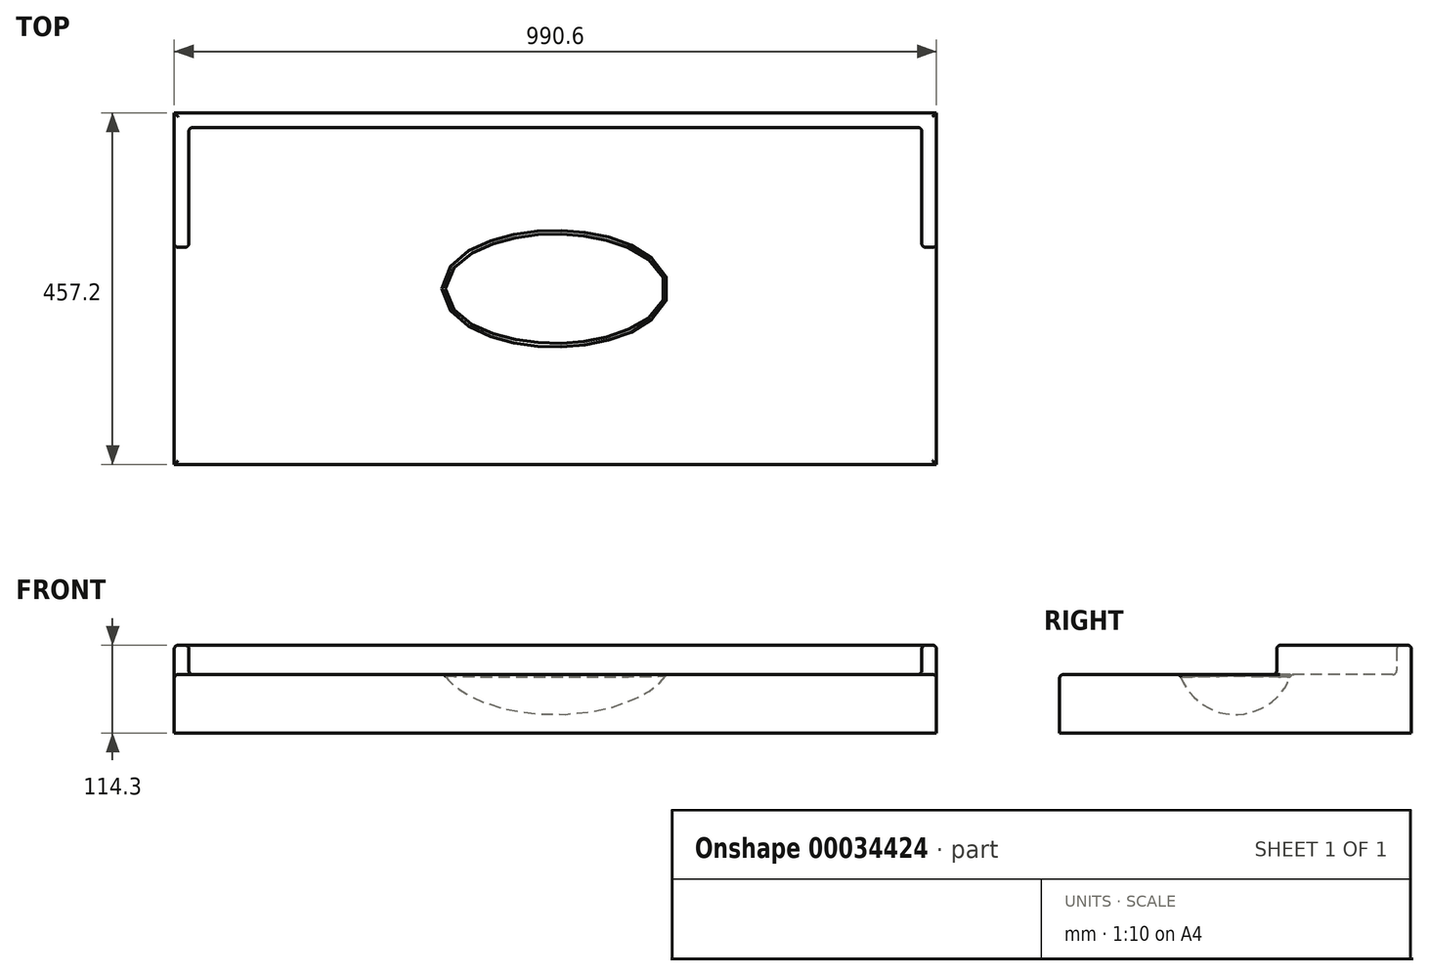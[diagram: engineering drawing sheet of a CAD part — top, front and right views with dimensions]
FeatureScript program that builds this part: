
annotation { "Feature Type Name" : "Feature", "Feature Type Description" : "" }
export const myFeature = defineFeature(function(context is Context, id is Id, definition is map)
    precondition{}
    {
        {
            var Q0;
            Q0=qCreatedBy(makeId("Top.planeOp"),FACE);
            var sketch = newSketch(context, id + "F0", { "sketchPlane" : qUnion([Q0])});
            skLineSegment(sketch, "E0.bottom", {"start": v(-495.3, 228.6) * mm, "end": v(495.3, 228.6) * mm});
            skLineSegment(sketch, "E0.top", {"start": v(-495.3, -228.6) * mm, "end": v(495.3, -228.6) * mm});
            skLineSegment(sketch, "E0.left", {"start": v(-495.3, 228.6) * mm, "end": v(-495.3, -228.6) * mm});
            skLineSegment(sketch, "E0.right", {"start": v(495.3, 228.6) * mm, "end": v(495.3, -228.6) * mm});
            skLineSegment(sketch, "E1", {"start": v(0, 228.6) * mm, "end": v(0, 0) * mm, "construction": true});
            skLineSegment(sketch, "E2", {"start": v(0, 0) * mm, "end": v(-495.3, 0) * mm, "construction": true});
            skSolve(sketch);
        }
        {
            var Q0;
            Q0=makeQuery(id+"F0.imprint","IMPRINT",FACE,{"disambiguationData":[TD([[makeQuery(id+"F0.imprint","IMPRINT",EDGE,{"derivedFrom":sQuery(id+"F0.wireOp",EDGE,"E0.bottom")}),-1.0]])]});
            extrude(context, id + "F1", {"entities" : qUnion([Q0]), "depth" : 76.2 * mm});
        }
        {
            var Q0;
            Q0=makeQuery(id+"F1.opExtrude","CAP_FACE",FACE,{"disambiguationData":[OSD([sQuery(id+"F0.wireOp",EDGE,"E0.bottom"),sQuery(id+"F0.wireOp",EDGE,"E0.top"),sQuery(id+"F0.wireOp",EDGE,"E0.left"),sQuery(id+"F0.wireOp",EDGE,"E0.right")])],"isStart":false});
            var sketch = newSketch(context, id + "F2", { "sketchPlane" : qUnion([Q0])});
            skLineSegment(sketch, "E3", {"start": v(-495.3, 53.68) * mm, "end": v(-476.25, 53.68) * mm});
            skLineSegment(sketch, "E4", {"start": v(-476.25, 53.68) * mm, "end": v(-476.25, 209.55) * mm});
            skLineSegment(sketch, "E5", {"start": v(-476.25, 209.55) * mm, "end": v(476.25, 209.55) * mm});
            skLineSegment(sketch, "E6", {"start": v(476.25, 209.55) * mm, "end": v(476.25, 53.68) * mm});
            skPoint(sketch, "E6.endSnap0", {"position": v(-485.78, 53.68) * mm});
            skLineSegment(sketch, "E7", {"start": v(476.25, 53.68) * mm, "end": v(495.3, 53.68) * mm});
            skLineSegment(sketch, "E8", {"start": v(495.3, 53.68) * mm, "end": v(495.3, 228.6) * mm});
            skLineSegment(sketch, "E9", {"start": v(495.3, 228.6) * mm, "end": v(-495.3, 228.6) * mm});
            skLineSegment(sketch, "E10", {"start": v(-495.3, 228.6) * mm, "end": v(-495.3, 53.68) * mm});
            skSolve(sketch);
        }
        {
            var Q0;
            Q0=makeQuery(id+"F2.imprint","IMPRINT",FACE,{"disambiguationData":[TD([[makeQuery(id+"F2.imprint","IMPRINT",EDGE,{"derivedFrom":sQuery(id+"F2.wireOp",EDGE,"E3")}),1.0]])]});
            extrude(context, id + "F3", {"entities" : qUnion([Q0]), "operationType" : NewBodyOperationType.ADD, "depth" : 38.1 * mm});
        }
        {
            var Q0;
            Q0=qCreatedBy(makeId("Front.planeOp"),FACE);
            var sketch = newSketch(context, id + "F4", { "sketchPlane" : qUnion([Q0])});
            skEllipticalArc(sketch, "E11", {});
            skLineSegment(sketch, "E12", {"start": v(-152.4, 100.33) * mm, "end": v(152.4, 100.33) * mm});
            const initialGuessF4  = {"E11": [0, 0.10033373534679413, 1, 0, 0.1524, 0.0762, 3.141592653589793, 0]};
            skSetInitialGuess(sketch, initialGuessF4);
            skSolve(sketch);
        }
        {
            var Q0;
            Q0 = qSketchRegion(id + "F4", true);
            var Q1;
            Q1=sQuery(id+"F4.wireOp",EDGE,"E12");
            revolve(context, id + "F5", {"operationType" : NewBodyOperationType.REMOVE, "entities" : qUnion([Q0]), "axis" : qUnion([Q1]), "revolveType" : RevolveType.FULL, "oppositeDirection" : true});
        }
        {
            var Q0;
            Q0=makeQuery(id+"F1.opExtrude","CAP_FACE",FACE,{"disambiguationData":[OSD([sQuery(id+"F0.wireOp",EDGE,"E0.bottom"),sQuery(id+"F0.wireOp",EDGE,"E0.top"),sQuery(id+"F0.wireOp",EDGE,"E0.left"),sQuery(id+"F0.wireOp",EDGE,"E0.right")])],"isStart":false});
            var Q1;
            Q1=makeQuery(id+"F3.opExtrude","CAP_FACE",FACE,{"disambiguationData":[OSD([sQuery(id+"F2.wireOp",EDGE,"E3"),sQuery(id+"F2.wireOp",EDGE,"E4"),sQuery(id+"F2.wireOp",EDGE,"E5"),sQuery(id+"F2.wireOp",EDGE,"E6"),sQuery(id+"F2.wireOp",EDGE,"E7"),sQuery(id+"F2.wireOp",EDGE,"E8"),sQuery(id+"F2.wireOp",EDGE,"E9"),sQuery(id+"F2.wireOp",EDGE,"E10")])],"isStart":false});
            var Q2;
            Q2=makeQuery(id+"F3.opExtrude","SWEPT_FACE",FACE,{"disambiguationData":[OSD([sQuery(id+"F2.wireOp",EDGE,"E3")])]});
            var Q3;
            Q3=makeQuery(id+"F3.opExtrude","SWEPT_FACE",FACE,{"disambiguationData":[OSD([sQuery(id+"F2.wireOp",EDGE,"E4")])]});
            var Q4;
            Q4=makeQuery(id+"F3.opExtrude","SWEPT_FACE",FACE,{"disambiguationData":[OSD([sQuery(id+"F2.wireOp",EDGE,"E5")])]});
            var Q5;
            Q5=makeQuery(id+"F3.opExtrude","SWEPT_FACE",FACE,{"disambiguationData":[OSD([sQuery(id+"F2.wireOp",EDGE,"E7")])]});
            fillet(context, id + "F6", {"entities" : qUnion([Q0, Q1, Q2, Q3, Q4, Q5]), "radius" : 5.08 * mm, "tangentPropagation" : true, "allowEdgeOverflow" : false});
        }
    });
